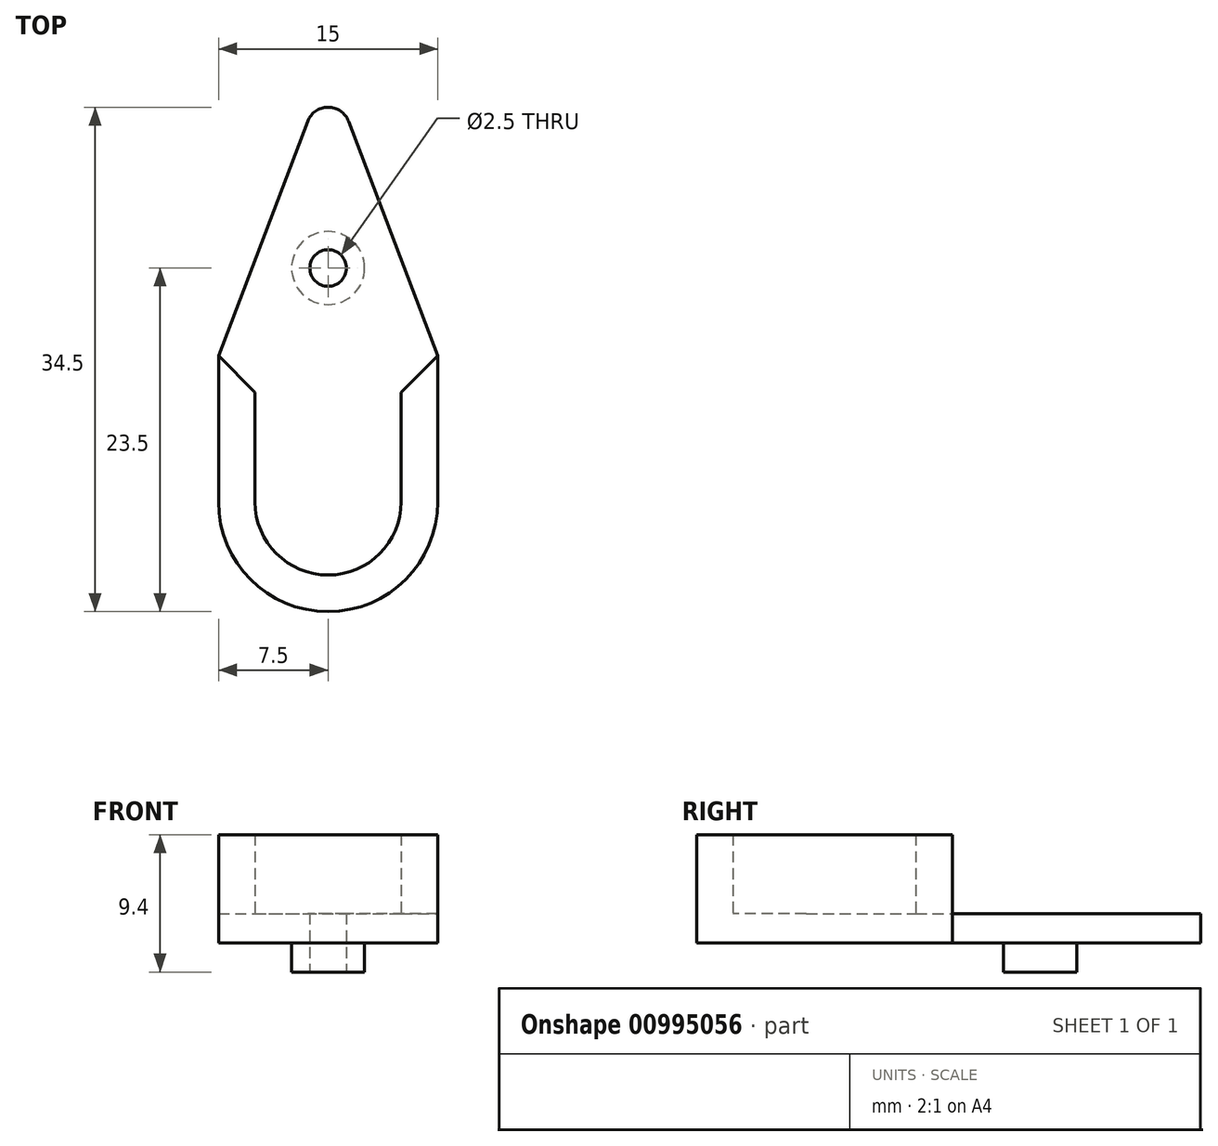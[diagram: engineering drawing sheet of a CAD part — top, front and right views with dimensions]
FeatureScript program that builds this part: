
annotation { "Feature Type Name" : "Feature", "Feature Type Description" : "" }
export const myFeature = defineFeature(function(context is Context, id is Id, definition is map)
    precondition{}
    {
        {
            var Q0;
            Q0=qCreatedBy(makeId("Top.planeOp"),FACE);
            var sketch = newSketch(context, id + "F0", { "sketchPlane" : qUnion([Q0])});
            skArc(sketch, "E0", {"start": v(-7.5, 0) * mm, "mid": v(0, -7.5) * mm, "end": v(7.5, 0) * mm});
            skLineSegment(sketch, "E1", {"start": v(-7.5, 0) * mm, "end": v(-7.5, 10) * mm});
            skLineSegment(sketch, "E2", {"start": v(7.5, 0) * mm, "end": v(7.5, 10) * mm});
            skArc(sketch, "E3", {"start": v(1.4, 26.03) * mm, "mid": v(0, 27) * mm, "end": v(-1.4, 26.03) * mm});
            skLineSegment(sketch, "E4", {"start": v(7.5, 10) * mm, "end": v(1.4, 26.03) * mm});
            skLineSegment(sketch, "E5", {"start": v(-7.5, 10) * mm, "end": v(-1.4, 26.03) * mm});
            skArc(sketch, "E6", {"start": v(-34.2, -9.26) * mm, "mid": v(-26.7, -16.76) * mm, "end": v(-19.2, -9.26) * mm});
            skLineSegment(sketch, "E7", {"start": v(-34.2, -9.26) * mm, "end": v(-34.2, 0.74) * mm});
            skLineSegment(sketch, "E8", {"start": v(-19.2, -9.26) * mm, "end": v(-19.2, 0.74) * mm});
            skLineSegment(sketch, "E9.0", {"start": v(-31.7, -9.26) * mm, "end": v(-31.7, -1.76) * mm});
            skArc(sketch, "E9.1", {"start": v(-31.7, -9.26) * mm, "mid": v(-26.7, -14.26) * mm, "end": v(-21.7, -9.26) * mm});
            skLineSegment(sketch, "E9.2", {"start": v(-21.7, -9.26) * mm, "end": v(-21.7, -1.76) * mm});
            skLineSegment(sketch, "E10", {"start": v(-21.7, -1.76) * mm, "end": v(-19.2, 0.74) * mm});
            skLineSegment(sketch, "E11", {"start": v(-34.2, 0.74) * mm, "end": v(-31.7, -1.76) * mm});
            skSolve(sketch);
        }
        {
            var Q0;
            Q0=makeQuery(id+"F0.imprint","IMPRINT",FACE,{"disambiguationData":[TD([[makeQuery(id+"F0.imprint","IMPRINT",EDGE,{"derivedFrom":sQuery(id+"F0.wireOp",EDGE,"E0")}),1.0]])]});
            extrude(context, id + "F1", {"entities" : qUnion([Q0]), "depth" : 2 * mm, "offsetDistance" : 25 * mm});
        }
        {
            var Q0;
            Q0=makeQuery(id+"F1.opExtrude","CAP_FACE",FACE,{"disambiguationData":[OSD([sQuery(id+"F0.wireOp",EDGE,"E0"),sQuery(id+"F0.wireOp",EDGE,"E1"),sQuery(id+"F0.wireOp",EDGE,"E2"),sQuery(id+"F0.wireOp",EDGE,"E3"),sQuery(id+"F0.wireOp",EDGE,"E4"),sQuery(id+"F0.wireOp",EDGE,"E5")])],"isStart":false});
            var sketch = newSketch(context, id + "F2", { "sketchPlane" : qUnion([Q0])});
            skArc(sketch, "E12", {"start": v(-7.5, 0) * mm, "mid": v(0, -7.5) * mm, "end": v(7.5, 0) * mm});
            skLineSegment(sketch, "E13", {"start": v(-7.5, 0) * mm, "end": v(-7.5, 10) * mm});
            skLineSegment(sketch, "E14", {"start": v(7.5, 0) * mm, "end": v(7.5, 10) * mm});
            skLineSegment(sketch, "E15.0", {"start": v(-5, 0) * mm, "end": v(-5, 7.5) * mm});
            skArc(sketch, "E15.1", {"start": v(-5, 0) * mm, "mid": v(0, -5) * mm, "end": v(5, 0) * mm});
            skLineSegment(sketch, "E15.2", {"start": v(5, 0) * mm, "end": v(5, 7.5) * mm});
            skLineSegment(sketch, "E16", {"start": v(5, 7.5) * mm, "end": v(7.5, 10) * mm});
            skLineSegment(sketch, "E17", {"start": v(-7.5, 10) * mm, "end": v(-5, 7.5) * mm});
            skSolve(sketch);
        }
        {
            var Q0;
            Q0 = qSketchRegion(id + "F2", true);
            extrude(context, id + "F3", {"entities" : qUnion([Q0]), "operationType" : NewBodyOperationType.ADD, "depth" : 5.4 * mm, "offsetDistance" : 25 * mm});
        }
        {
            var Q0;
            Q0=makeQuery(id+"F1.opExtrude","CAP_FACE",FACE,{"disambiguationData":[OSD([sQuery(id+"F0.wireOp",EDGE,"E0"),sQuery(id+"F0.wireOp",EDGE,"E1"),sQuery(id+"F0.wireOp",EDGE,"E2"),sQuery(id+"F0.wireOp",EDGE,"E3"),sQuery(id+"F0.wireOp",EDGE,"E4"),sQuery(id+"F0.wireOp",EDGE,"E5")])],"isStart":true});
            var sketch = newSketch(context, id + "F4", { "sketchPlane" : qUnion([Q0])});
            skCircle(sketch, "E18", {"center": v(0, -16) * mm, "radius": 2.5 * mm});
            skSolve(sketch);
        }
        {
            var Q0;
            Q0 = qSketchRegion(id + "F4", true);
            extrude(context, id + "F5", {"entities" : qUnion([Q0]), "operationType" : NewBodyOperationType.ADD, "depth" : 2 * mm, "offsetDistance" : 25 * mm});
        }
        {
            var Q0;
            Q0=makeQuery(id+"F5.opExtrude","CAP_FACE",FACE,{"disambiguationData":[OSD([sQuery(id+"F4.wireOp",EDGE,"E18")])],"isStart":false});
            var sketch = newSketch(context, id + "F6", { "sketchPlane" : qUnion([Q0])});
            skCircle(sketch, "E19", {"center": v(0, -16) * mm, "radius": 1.25 * mm});
            skSolve(sketch);
        }
        {
            var Q0;
            Q0 = qSketchRegion(id + "F6", true);
            extrude(context, id + "F7", {"entities" : qUnion([Q0]), "operationType" : NewBodyOperationType.REMOVE, "oppositeDirection" : true, "depth" : 25 * mm, "offsetDistance" : 25 * mm});
        }
    });
